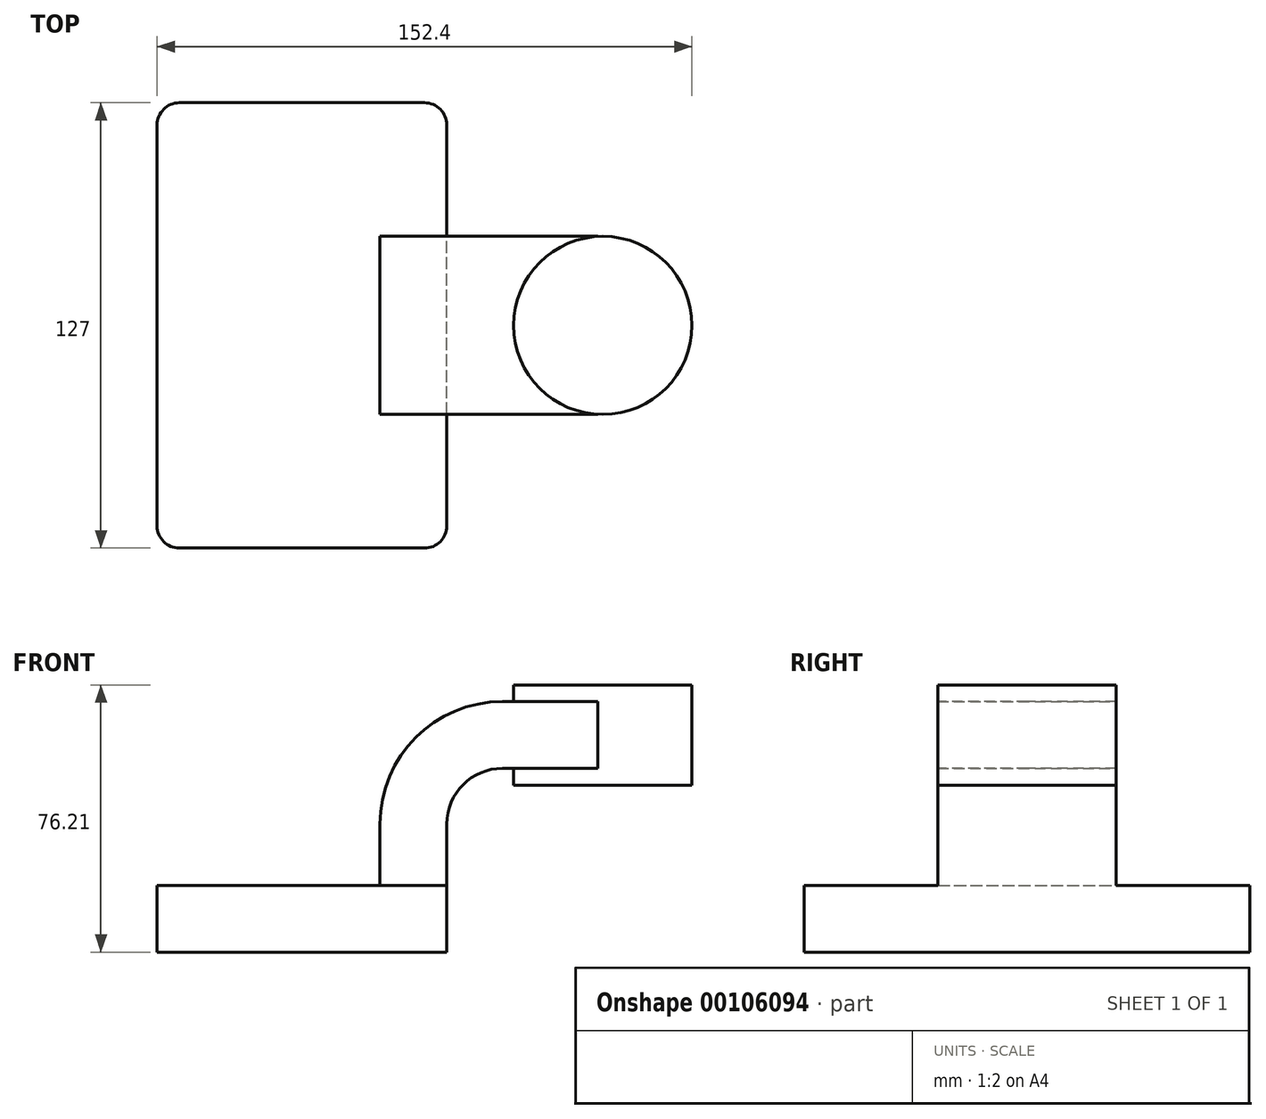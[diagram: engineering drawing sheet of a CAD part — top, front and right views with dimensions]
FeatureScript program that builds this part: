
annotation { "Feature Type Name" : "Feature", "Feature Type Description" : "" }
export const myFeature = defineFeature(function(context is Context, id is Id, definition is map)
    precondition{}
    {
        {
            var Q0;
            Q0=qCreatedBy(makeId("Front.planeOp"),FACE);
            var sketch = newSketch(context, id + "F0", { "sketchPlane" : qUnion([Q0])});
            skLineSegment(sketch, "E0.bottom", {"start": v(-41.28, -9.53) * mm, "end": v(41.28, -9.53) * mm});
            skLineSegment(sketch, "E0.top", {"start": v(-41.28, 9.53) * mm, "end": v(41.28, 9.53) * mm});
            skLineSegment(sketch, "E0.left", {"start": v(-41.28, -9.53) * mm, "end": v(-41.28, 9.53) * mm});
            skLineSegment(sketch, "E0.right", {"start": v(41.28, -9.53) * mm, "end": v(41.28, 9.53) * mm});
            skPoint(sketch, "E0.middle", {"position": v(0, 0) * mm});
            skLineSegment(sketch, "E1.bottom", {"start": v(60.33, 38.1) * mm, "end": v(111.12, 38.1) * mm});
            skLineSegment(sketch, "E1.top", {"start": v(60.32, 66.67) * mm, "end": v(111.12, 66.67) * mm});
            skLineSegment(sketch, "E1.left", {"start": v(60.32, 38.1) * mm, "end": v(60.32, 66.67) * mm});
            skLineSegment(sketch, "E1.right", {"start": v(111.12, 38.1) * mm, "end": v(111.12, 66.67) * mm});
            skPoint(sketch, "E1.middle", {"position": v(85.72, 52.39) * mm});
            skLineSegment(sketch, "E2", {"start": v(41.28, 9.52) * mm, "end": v(41.28, 27) * mm});
            skArc(sketch, "E3", {"start": v(41.27, 27) * mm, "mid": v(45.92, 38.23) * mm, "end": v(57.15, 42.88) * mm});
            skLineSegment(sketch, "E4", {"start": v(57.15, 42.88) * mm, "end": v(84.3, 42.88) * mm});
            skLineSegment(sketch, "E5.0", {"start": v(57.15, 61.93) * mm, "end": v(84.3, 61.93) * mm});
            skArc(sketch, "E5.1", {"start": v(22.22, 27) * mm, "mid": v(32.45, 51.7) * mm, "end": v(57.15, 61.93) * mm});
            skLineSegment(sketch, "E5.2", {"start": v(22.22, 9.52) * mm, "end": v(22.22, 27) * mm});
            skLineSegment(sketch, "E6", {"start": v(84.3, 42.88) * mm, "end": v(84.3, 61.93) * mm});
            skFitSpline(sketch, "E7", {"points": [v(-41.28, 9.53) * mm, v(57.15, 61.93) * mm], "startDerivative": vector(69.49, 139.8) * mm, "endDerivative": vector(106.67, -5.3) * mm});
            skLineSegment(sketch, "E8", {"start": v(85.72, 52.39) * mm, "end": v(85.72, 70.07) * mm});
            skLineSegment(sketch, "E9", {"start": v(85.72, 52.39) * mm, "end": v(85.72, 34.24) * mm});
            skSolve(sketch);
        }
        {
            var Q0;
            Q0=makeQuery(id+"F0.imprint","IMPRINT",FACE,{"disambiguationData":[TD([[makeQuery(id+"F0.imprint","IMPRINT",EDGE,{"derivedFrom":sQuery(id+"F0.wireOp",EDGE,"E0.bottom")}),1.0]])]});
            extrude(context, id + "F1", {"entities" : qUnion([Q0]), "endBound" : BoundingType.SYMMETRIC, "depth" : 127 * mm});
        }
        {
            var Q0;
            {var subQ1=sQuery(id+"F0.wireOp",EDGE,"E2");Q0=makeQuery(id+"F0.imprint","IMPRINT",FACE,{"disambiguationData":[TD([[makeQuery(id+"F0.imprint","IMPRINT",EDGE,{"derivedFrom":subQ1}),1.0]])]});}
            var Q1;
            {var subQ5=sQuery(id+"F0.wireOp",EDGE,"E6");Q1=makeQuery(id+"F0.imprint","IMPRINT",FACE,{"disambiguationData":[TD([[makeQuery(id+"F0.imprint","IMPRINT",EDGE,{"derivedFrom":subQ5}),1.0]])]});}
            extrude(context, id + "F2", {"entities" : qUnion([Q0, Q1]), "operationType" : NewBodyOperationType.ADD, "endBound" : BoundingType.SYMMETRIC, "depth" : 50.8 * mm});
        }
        {
            var Q0;
            Q0=makeQuery(id+"F0.imprint","IMPRINT",FACE,{"disambiguationData":[TD([[makeQuery(id+"F0.imprint","IMPRINT",EDGE,{"derivedFrom":sQuery(id+"F0.wireOp",EDGE,"E5.1")}),1.0]])]});
            extrude(context, id + "F3", {"entities" : qUnion([Q0]), "operationType" : NewBodyOperationType.ADD, "endBound" : BoundingType.SYMMETRIC, "depth" : 25.4 * mm});
        }
        {
            var Q0;
            {var subQ5=sQuery(id+"F0.wireOp",EDGE,"E1.right");Q0=makeQuery(id+"F0.imprint","IMPRINT",FACE,{"disambiguationData":[TD([[makeQuery(id+"F0.imprint","IMPRINT",EDGE,{"derivedFrom":subQ5}),1.0]])]});}
            var Q1;
            Q1=sQuery(id+"F0.wireOp",EDGE,"E8");
            revolve(context, id + "F4", {"operationType" : NewBodyOperationType.ADD, "entities" : qUnion([Q0]), "axis" : qUnion([Q1]), "revolveType" : RevolveType.FULL});
        }
        {
            var Q0;
            Q0=makeQuery(id+"F1.opExtrude","CAP_EDGE",EDGE,{"disambiguationData":[OSD([sQuery(id+"F0.wireOp",EDGE,"E0.right")])],"isStart":false});
            var Q1;
            Q1=makeQuery(id+"F1.opExtrude","CAP_EDGE",EDGE,{"disambiguationData":[OSD([sQuery(id+"F0.wireOp",EDGE,"E0.left")])],"isStart":false});
            var Q2;
            Q2=makeQuery(id+"F1.opExtrude","CAP_EDGE",EDGE,{"disambiguationData":[OSD([sQuery(id+"F0.wireOp",EDGE,"E0.right")])],"isStart":true});
            var Q3;
            Q3=makeQuery(id+"F1.opExtrude","CAP_EDGE",EDGE,{"disambiguationData":[OSD([sQuery(id+"F0.wireOp",EDGE,"E0.left")])],"isStart":true});
            fillet(context, id + "F5", {"entities" : qUnion([Q0, Q1, Q2, Q3]), "radius" : 6.35 * mm, "tangentPropagation" : true, "allowEdgeOverflow" : false});
        }
    });
